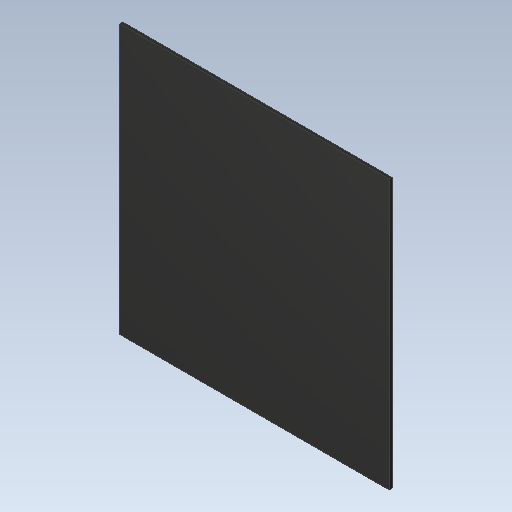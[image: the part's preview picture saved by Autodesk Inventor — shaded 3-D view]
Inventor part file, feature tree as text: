
AUTODESK INVENTOR PART (.ipt)
format: ipt  version: 2023 (Build 270158000, 158)  size: 91,136 bytes
history: imported  units: in
note: dims shown in document units (in); Inventor stores cm internally (conversion verified against a paired STEP export)
features: imported_body x1
ambient origin geometry x8: Origin, YZ Plane, XZ Plane, XY Plane, X Axis, Y Axis, Z Axis, Center Point
bodies: Solid1 (imported_parasolid), Body1 (imported_parasolid)
feature tree (1):
  imported_body  NMx_Import_Brep_tag  [imported B-rep: ~6 faces, bbox_mm=[9.8552, 9.8552, 0.1]]
